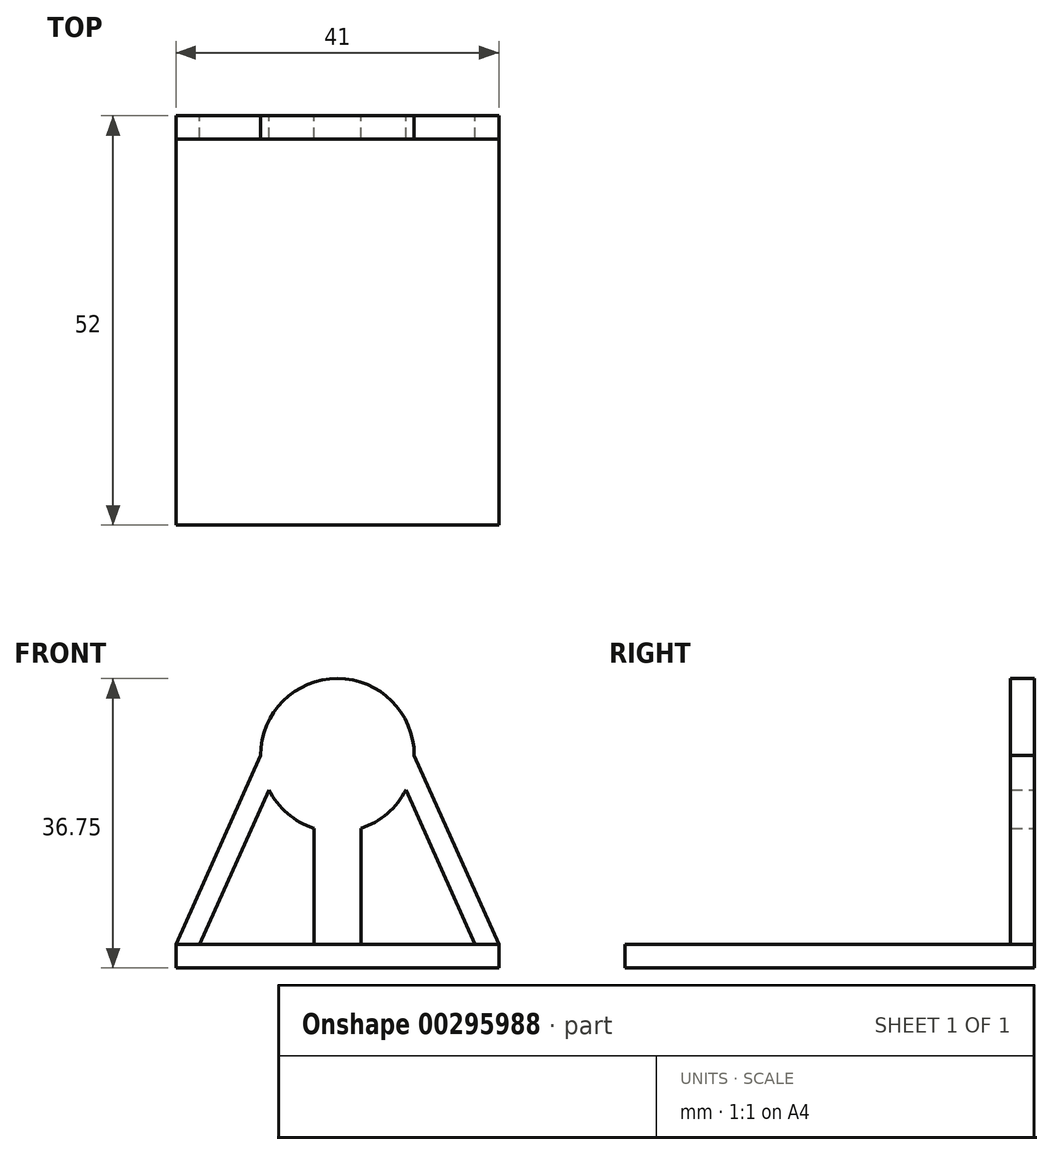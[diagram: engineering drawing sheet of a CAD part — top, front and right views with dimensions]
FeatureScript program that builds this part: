
annotation { "Feature Type Name" : "Feature", "Feature Type Description" : "" }
export const myFeature = defineFeature(function(context is Context, id is Id, definition is map)
    precondition{}
    {
        {
            var Q0;
            Q0=qCreatedBy(makeId("Top.planeOp"),FACE);
            var sketch = newSketch(context, id + "F0", { "sketchPlane" : qUnion([Q0])});
            skLineSegment(sketch, "E0.bottom", {"start": v(6.5, 18.44) * mm, "end": v(47.5, 18.44) * mm});
            skLineSegment(sketch, "E0.top", {"start": v(6.5, -33.56) * mm, "end": v(47.5, -33.56) * mm});
            skLineSegment(sketch, "E0.left", {"start": v(6.5, 18.44) * mm, "end": v(6.5, -33.56) * mm});
            skLineSegment(sketch, "E0.right", {"start": v(47.5, 18.44) * mm, "end": v(47.5, -33.56) * mm});
            skSolve(sketch);
        }
        {
            var Q0;
            Q0=makeQuery(id+"F0.imprint","IMPRINT",FACE,{"disambiguationData":[TD([[makeQuery(id+"F0.imprint","IMPRINT",EDGE,{"derivedFrom":sQuery(id+"F0.wireOp",EDGE,"E0.bottom")}),-1.0]])]});
            extrude(context, id + "F1", {"entities" : qUnion([Q0]), "depth" : 3 * mm});
        }
        {
            var Q0;
            Q0=makeQuery(id+"F1.opExtrude","SWEPT_FACE",FACE,{"disambiguationData":[OSD([sQuery(id+"F0.wireOp",EDGE,"E0.bottom")])]});
            var sketch = newSketch(context, id + "F2", { "sketchPlane" : qUnion([Q0])});
            skLineSegment(sketch, "E1.bottom", {"start": v(-47.5, 0) * mm, "end": v(-6.5, 0) * mm});
            skCircle(sketch, "E2", {"center": v(-27, 27) * mm, "radius": 9.75 * mm});
            skLineSegment(sketch, "E3", {"start": v(-36.75, 27) * mm, "end": v(-47.5, 3) * mm});
            skLineSegment(sketch, "E4", {"start": v(-17.25, 27) * mm, "end": v(-6.5, 3) * mm});
            skLineSegment(sketch, "E5", {"start": v(-27, 17.25) * mm, "end": v(-27, 3) * mm});
            skLineSegment(sketch, "E6", {"start": v(-27, 3) * mm, "end": v(-24, 3) * mm});
            skLineSegment(sketch, "E7", {"start": v(-24, 3) * mm, "end": v(-30, 3) * mm});
            skLineSegment(sketch, "E8", {"start": v(-30, 3) * mm, "end": v(-30, 17.72) * mm});
            skLineSegment(sketch, "E9", {"start": v(-24, 3) * mm, "end": v(-24, 17.72) * mm});
            skLineSegment(sketch, "E10", {"start": v(-47.5, 3) * mm, "end": v(-44.5, 3) * mm});
            skLineSegment(sketch, "E11", {"start": v(-44.5, 3) * mm, "end": v(-35.71, 22.62) * mm});
            skLineSegment(sketch, "E12", {"start": v(-18.29, 22.62) * mm, "end": v(-9.5, 3) * mm});
            skSolve(sketch);
        }
        {
            var Q0;
            Q0 = qSketchRegion(id + "F2", true);
            var Q1;
            {var subQ0=sQuery(id+"F2.wireOp",EDGE,"E4");Q1=makeQuery(id+"F2.imprint","IMPRINT",FACE,{"disambiguationData":[TD([[makeQuery(id+"F2.imprint","IMPRINT",EDGE,{"derivedFrom":subQ0}),-1.0]])]});}
            extrude(context, id + "F3", {"entities" : qUnion([Q0, Q1]), "operationType" : NewBodyOperationType.ADD, "oppositeDirection" : true, "depth" : 3 * mm});
        }
    });
